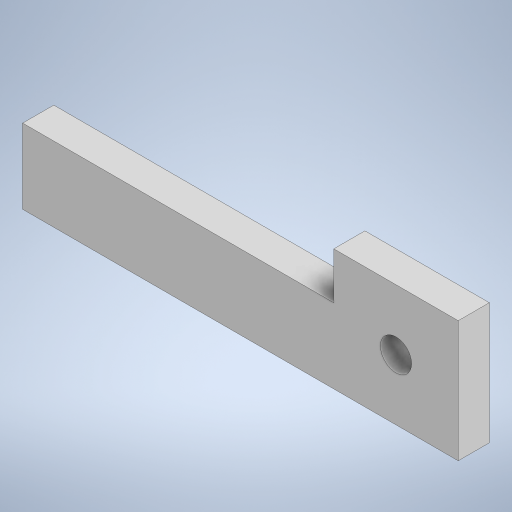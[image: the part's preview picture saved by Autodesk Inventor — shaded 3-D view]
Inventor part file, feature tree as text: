
AUTODESK INVENTOR PART (.ipt)
format: ipt  version: 2023 (Build 270158000, 158)  size: 221,184 bytes
history: native  units: in
note: dims shown in document units (in); Inventor stores cm internally (conversion verified against a paired STEP export)
features: extrude x1, sketch x1
ambient origin geometry x8: Origin, YZ Plane, XZ Plane, XY Plane, X Axis, Y Axis, Z Axis, Center Point
bodies: Body1 (feature_tree)
feature tree (2):
  extrude  "Extrusion2"  Depth=0.4724in
  sketch  "Sketch1"  dims[d0=2.7559in d1=0.4724in d11=0.7874in d12=0.2953in d15=0.3839in d16=0.3937in d17=0.1969in d18=0.1969in d19=0.0in]
